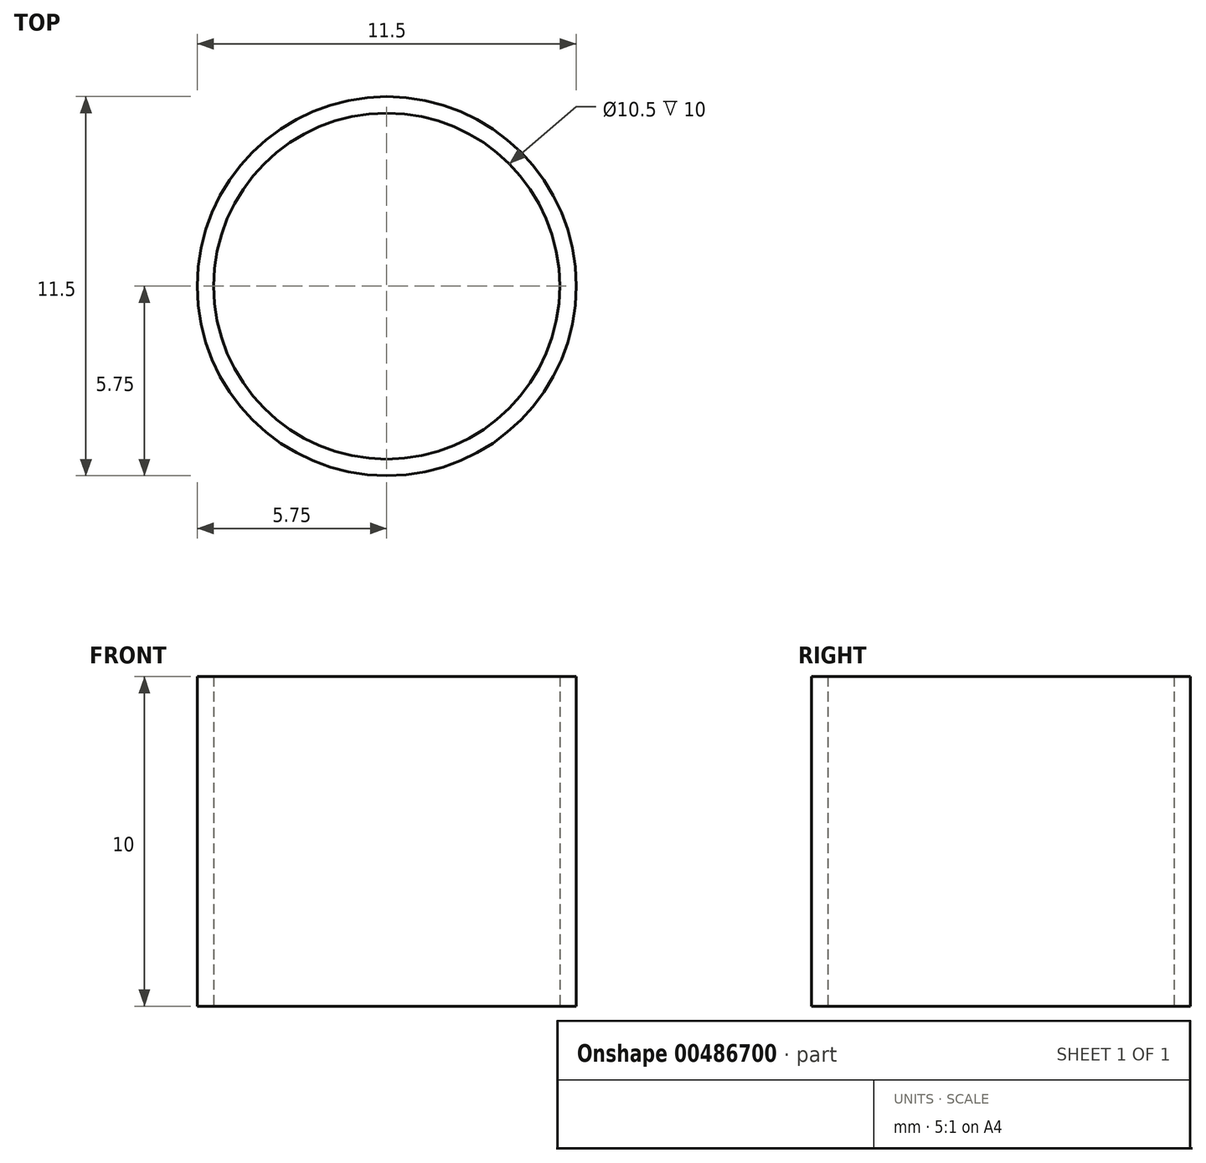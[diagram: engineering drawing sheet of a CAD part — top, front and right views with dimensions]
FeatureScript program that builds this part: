
annotation { "Feature Type Name" : "Feature", "Feature Type Description" : "" }
export const myFeature = defineFeature(function(context is Context, id is Id, definition is map)
    precondition{}
    {
        {
            var Q0;
            Q0=qCreatedBy(makeId("Top.planeOp"),FACE);
            var sketch = newSketch(context, id + "F0", { "sketchPlane" : qUnion([Q0])});
            skCircle(sketch, "E0", {"center": v(0, 0) * mm, "radius": 5.75 * mm});
            skCircle(sketch, "E1", {"center": v(0, 0) * mm, "radius": 5.25 * mm});
            skSolve(sketch);
        }
        {
            var Q0;
            Q0=makeQuery(id+"F0.imprint","IMPRINT",FACE,{"disambiguationData":[TD([[makeQuery(id+"F0.imprint","IMPRINT",EDGE,{"derivedFrom":sQuery(id+"F0.wireOp",EDGE,"E0")}),1.0]])]});
            extrude(context, id + "F1", {"entities" : qUnion([Q0]), "depth" : 10 * mm});
        }
    });
